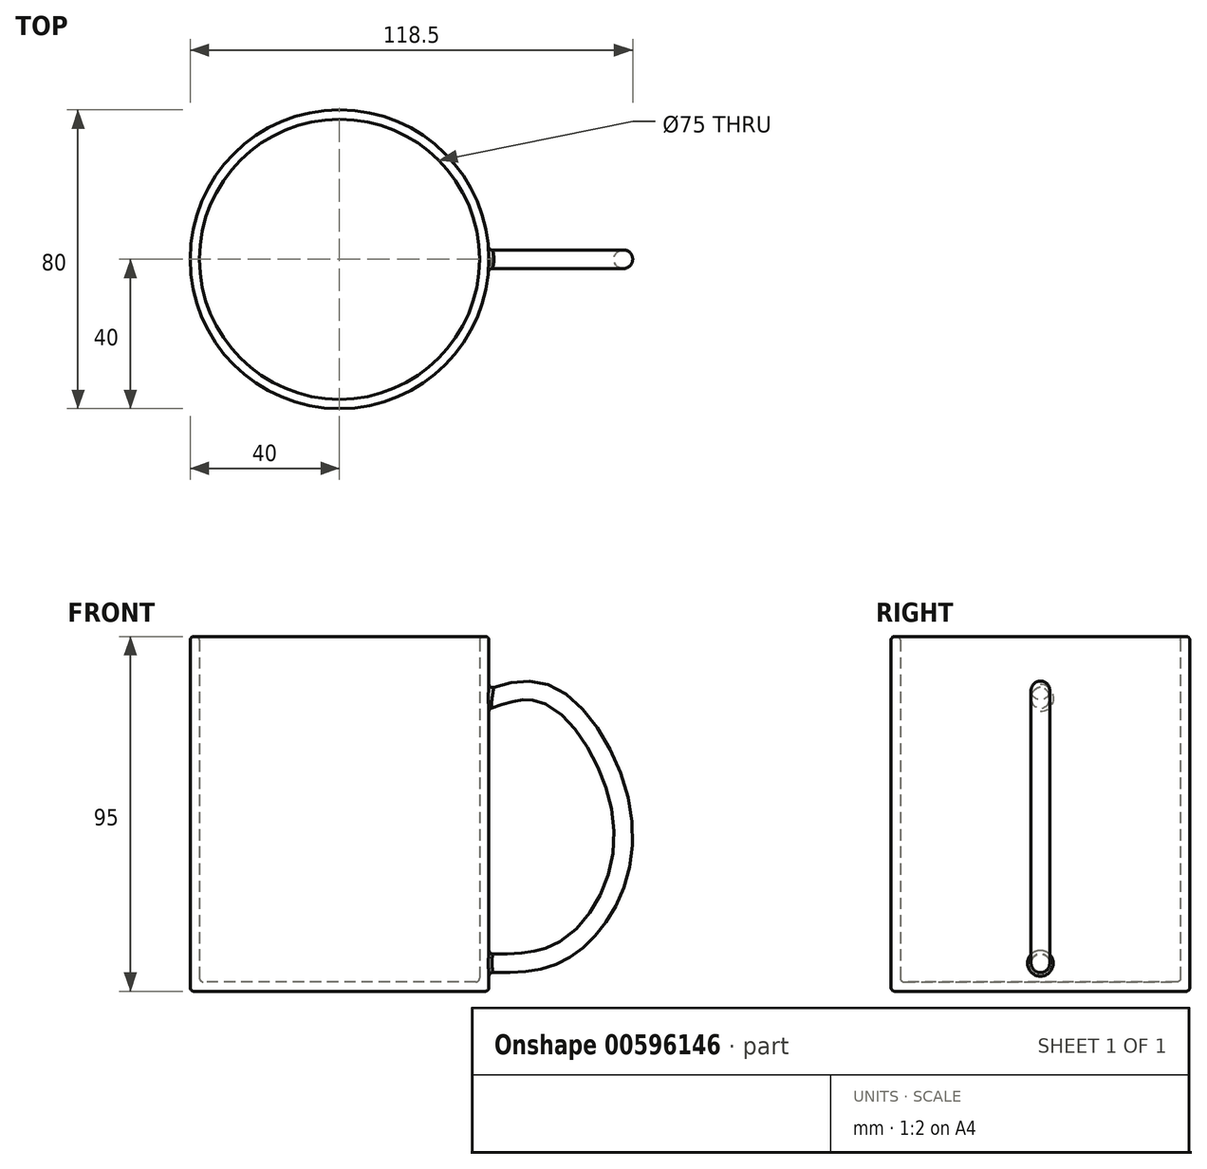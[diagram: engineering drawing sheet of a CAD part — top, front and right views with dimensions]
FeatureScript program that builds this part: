
annotation { "Feature Type Name" : "Feature", "Feature Type Description" : "" }
export const myFeature = defineFeature(function(context is Context, id is Id, definition is map)
    precondition{}
    {
        {
            var Q0;
            Q0=qCreatedBy(makeId("Top.planeOp"),FACE);
            var sketch = newSketch(context, id + "F0", { "sketchPlane" : qUnion([Q0])});
            skCircle(sketch, "E0", {"center": v(0, 0) * mm, "radius": 40 * mm});
            skSolve(sketch);
        }
        {
            var Q0;
            Q0 = qSketchRegion(id + "F0", true);
            extrude(context, id + "F1", {"entities" : qUnion([Q0]), "depth" : 95 * mm, "offsetDistance" : 25 * mm});
        }
        {
            var Q0;
            Q0=qCreatedBy(makeId("Right.planeOp"),FACE);
            cPlane(context, id + "F2", {"entities" : qUnion([Q0]), "cplaneType" : CPlaneType.OFFSET, "offset" : 40 * mm, "width" : 150 * mm, "height" : 150 * mm});
        }
        {
            var Q0;
            Q0=qCreatedBy(makeId("Front.planeOp"),FACE);
            var sketch = newSketch(context, id + "F3", { "sketchPlane" : qUnion([Q0])});
            skFitSpline(sketch, "E1", {"points": [v(36.06, 76.45) * mm, v(56.2, 79.1) * mm, v(75.55, 46.58) * mm, v(68.02, 18.4) * mm, v(54.32, 8.79) * mm, v(37.12, 7.78) * mm], "startDerivative": vector(109.58, 46.22) * mm, "endDerivative": vector(-104.5, 4.14) * mm});
            skSolve(sketch);
        }
        {
            var Q0;
            Q0=qCreatedBy(id+"F2.planeOp",FACE);
            var sketch = newSketch(context, id + "F4", { "sketchPlane" : qUnion([Q0])});
            skCircle(sketch, "E2", {"center": v(0, 7.55) * mm, "radius": 2.5 * mm});
            skSolve(sketch);
        }
        {
            var Q0;
            Q0=makeQuery(id+"F4.imprint","IMPRINT",FACE,{"disambiguationData":[TD([[makeQuery(id+"F4.imprint","IMPRINT",EDGE,{"derivedFrom":sQuery(id+"F4.wireOp",EDGE,"E2")}),1.0]])]});
            var Q1;
            Q1 = qConstructionFilter(qBodyType(qCreatedBy(id + "F3" ,EDGE), BodyType.WIRE), ConstructionObject.NO);
            sweep(context, id + "F5", {"operationType" : NewBodyOperationType.ADD, "profiles" : qUnion([Q0]), "path" : qUnion([Q1])});
        }
        {
            var Q0;
            Q0=makeQuery(id+"F1.opExtrude","CAP_FACE",FACE,{"disambiguationData":[OSD([sQuery(id+"F0.wireOp",EDGE,"E0")])],"isStart":false});
            shell(context, id + "F6", {"entities" : qUnion([Q0]), "thickness" : 2.5 * mm});
        }
        {
            var Q0;
            Q0=makeQuery(id+"F1.opExtrude","CAP_EDGE",EDGE,{"disambiguationData":[OSD([sQuery(id+"F0.wireOp",EDGE,"E0")])],"isStart":false});
            fillet(context, id + "F7", {"entities" : qUnion([Q0]), "radius" : 1 * mm, "tangentPropagation" : true, "allowEdgeOverflow" : false});
        }
        {
            var Q0;
            {var subQ0=sQuery(id+"F0.wireOp",EDGE,"E0");Q0=makeQuery(id+"F6.opShell","OFFSET_EDGE",EDGE,{"disambiguationData":[OSD([subQ0]),TDD([makeQuery(id+"F1.opExtrude","CAP_EDGE",EDGE,{"disambiguationData":[OSD([subQ0])],"isStart":false})])]});}
            fillet(context, id + "F8", {"entities" : qUnion([Q0]), "radius" : 1 * mm, "tangentPropagation" : true, "allowEdgeOverflow" : false});
        }
        {
            var Q0;
            Q0=makeQuery(id+"F1.opExtrude","CAP_FACE",FACE,{"disambiguationData":[OSD([sQuery(id+"F0.wireOp",EDGE,"E0")])],"isStart":true});
            var Q1;
            Q1=makeQuery(id+"F5.boolean.opBoolean","INTERSECT",EDGE,{"disambiguationData":[OD(0.0)],"derivedFrom":[makeQuery(id+"F1.opExtrude","SWEPT_FACE",FACE,{"disambiguationData":[OSD([sQuery(id+"F0.wireOp",EDGE,"E0")])]}),makeQuery(id+"F5.opSweep","SWEPT_FACE",FACE,{"disambiguationData":[OSD([sQuery(id+"F3.wireOp",EDGE,"E1"),sQuery(id+"F4.wireOp",EDGE,"E2")])]})]});
            fillet(context, id + "F9", {"entities" : qUnion([Q0, Q1]), "radius" : 1 * mm, "tangentPropagation" : true, "allowEdgeOverflow" : false});
        }
        {
            var Q0;
            Q0=makeQuery(id+"F5.boolean.opBoolean","INTERSECT",EDGE,{"disambiguationData":[OD(1.0)],"derivedFrom":[makeQuery(id+"F1.opExtrude","SWEPT_FACE",FACE,{"disambiguationData":[OSD([sQuery(id+"F0.wireOp",EDGE,"E0")])]}),makeQuery(id+"F5.opSweep","SWEPT_FACE",FACE,{"disambiguationData":[OSD([sQuery(id+"F3.wireOp",EDGE,"E1"),sQuery(id+"F4.wireOp",EDGE,"E2")])]})]});
            fillet(context, id + "F10", {"entities" : qUnion([Q0]), "radius" : 1 * mm, "tangentPropagation" : true, "allowEdgeOverflow" : false});
        }
        {
            var Q0;
            {var subQ0=sQuery(id+"F0.wireOp",EDGE,"E0");Q0=makeQuery(id+"F6.opShell","OFFSET_EDGE",EDGE,{"disambiguationData":[OSD([subQ0]),TDD([makeQuery(id+"F1.opExtrude","CAP_EDGE",EDGE,{"disambiguationData":[OSD([subQ0])],"isStart":true})])]});}
            fillet(context, id + "F11", {"entities" : qUnion([Q0]), "radius" : 1 * mm, "tangentPropagation" : true, "allowEdgeOverflow" : false});
        }
    });
